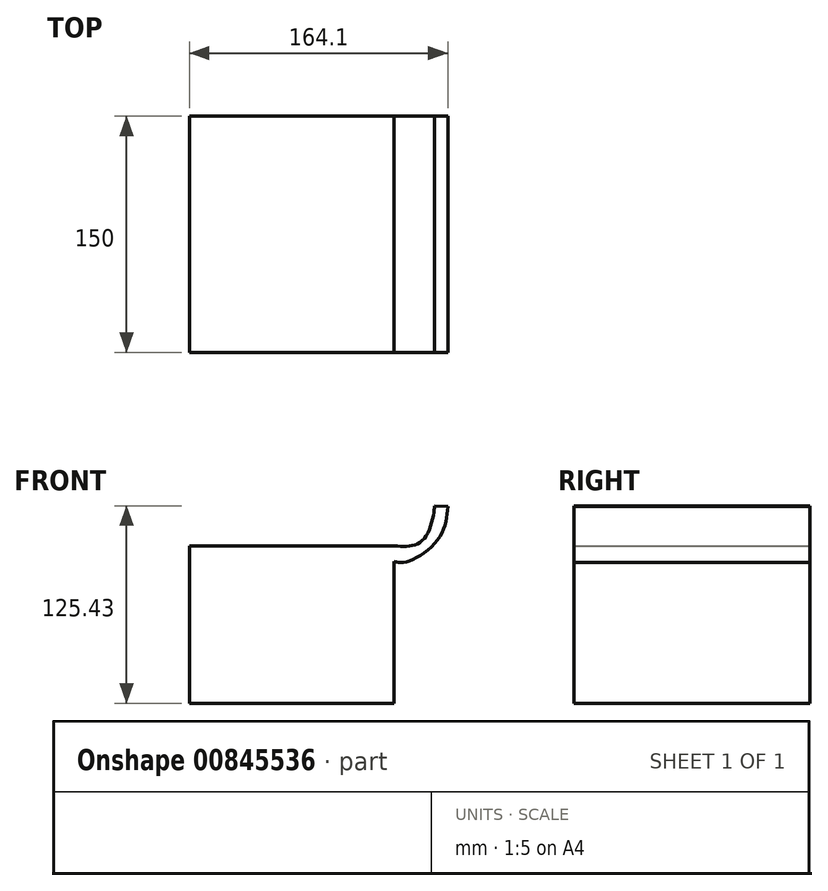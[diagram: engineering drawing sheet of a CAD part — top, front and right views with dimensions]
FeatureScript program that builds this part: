
annotation { "Feature Type Name" : "Feature", "Feature Type Description" : "" }
export const myFeature = defineFeature(function(context is Context, id is Id, definition is map)
    precondition{}
    {
        {
            var Q0;
            Q0=qCreatedBy(makeId("Front.planeOp"),FACE);
            var sketch = newSketch(context, id + "F0", { "sketchPlane" : qUnion([Q0])});
            skLineSegment(sketch, "E0.bottom", {"start": v(-63.45, 53.23) * mm, "end": v(66.55, 53.23) * mm});
            skLineSegment(sketch, "E0.top", {"start": v(-63.45, -46.77) * mm, "end": v(66.55, -46.77) * mm});
            skLineSegment(sketch, "E0.left", {"start": v(-63.45, 53.23) * mm, "end": v(-63.45, -46.77) * mm});
            skLineSegment(sketch, "E0.right", {"start": v(66.55, 43.44) * mm, "end": v(66.55, -46.77) * mm});
            skFitSpline(sketch, "E1", {"points": [v(66.55, 53.23) * mm, v(86.23, 58.58) * mm, v(92.07, 78.66) * mm, v(91.9, 78.48) * mm], "startDerivative": vector(48.12, -2.98) * mm, "endDerivative": vector(-3.91, -6.45) * mm});
            skFitSpline(sketch, "E2", {"points": [v(66.55, 43.44) * mm, v(75.1, 43.25) * mm, v(95.18, 58.4) * mm, v(100.65, 78.3) * mm], "startDerivative": vector(31.94, -7.61) * mm, "endDerivative": vector(4.9, 55.9) * mm});
            skLineSegment(sketch, "E3", {"start": v(92.07, 78.66) * mm, "end": v(100.65, 78.3) * mm});
            skSolve(sketch);
        }
        {
            var Q0;
            Q0 = qSketchRegion(id + "F0", true);
            extrude(context, id + "F1", {"entities" : qUnion([Q0]), "depth" : 150 * mm, "offsetDistance" : 25 * mm});
        }
    });
